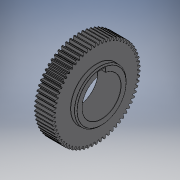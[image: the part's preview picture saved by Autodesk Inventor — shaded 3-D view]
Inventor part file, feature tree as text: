
AUTODESK INVENTOR PART (.ipt)
format: ipt  version: 2018 (Build 220112000, 112)  size: 1,100,288 bytes
history: native  units: mm
features: extrude x3, sketch x3, fillet x2, chamfer x1
ambient origin geometry x8: Origin, YZ Plane, XZ Plane, XY Plane, X Axis, Y Axis, Z Axis, Center Point
bodies: Solid1 (feature_tree)
feature tree (9):
  extrude  "Extrusion1"  Depth=31.76mm
  extrude  "Extrusion2"  Depth=0.57mm
  chamfer  "Chamfer1"  Distance=0.2mm
  fillet  "Fillet1"  Radius=6.39mm
  extrude  "Extrusion3"  Depth=0.1mm TaperAngle=360.0deg
  fillet  "Fillet2"  Radius=7.0mm
  sketch  "Sketch1"  dims[d0=15.0mm d1=31.76mm d2=34.0mm]
  sketch  "Sketch2"  dims[d3=0.135mm d4=0.57mm]
  sketch  "Sketch3"  dims[d5=0.2mm d6=0.2mm d7=6.39mm d8=660.0mm d10=360.0deg d12=7.0mm d13=0.0mm d14=20.0mm d15=2.0mm d16=0.0mm d17=0.5mm d18=2.0mm d19=45.0deg d20=0.1mm d21=9.0mm d22=3.0mm d23=20.5mm d24=0.0mm d25=0.1mm]
